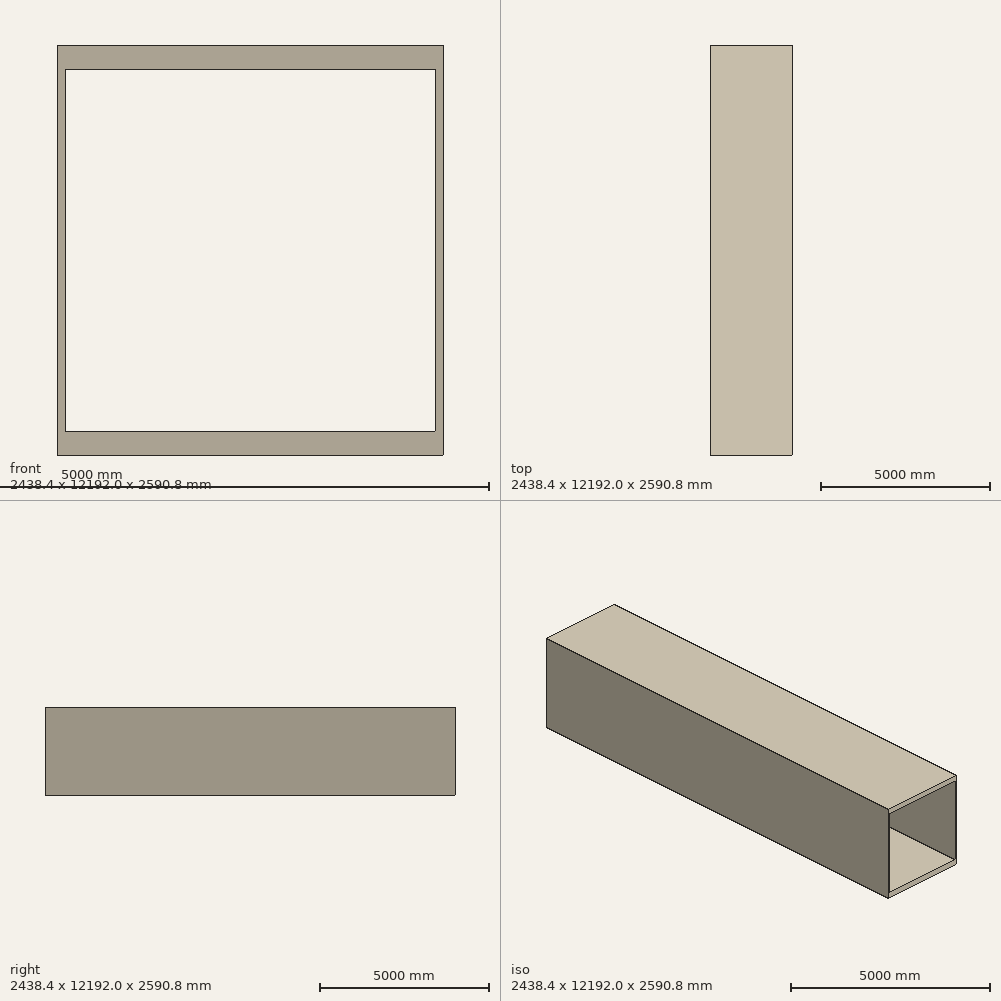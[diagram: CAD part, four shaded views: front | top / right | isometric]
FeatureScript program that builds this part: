
annotation { "Feature Type Name" : "Feature", "Feature Type Description" : "" }
export const myFeature = defineFeature(function(context is Context, id is Id, definition is map)
    precondition{}
    {
        {
            var Q0;
            Q0=qCreatedBy(makeId("Front.planeOp"),FACE);
            var sketch = newSketch(context, id + "F0", { "sketchPlane" : qUnion([Q0])});
            skLineSegment(sketch, "E0.bottom", {"start": v(-1219.2, 0) * mm, "end": v(1219.2, 0) * mm});
            skLineSegment(sketch, "E0.top", {"start": v(-1219.2, 2590.8) * mm, "end": v(1219.2, 2590.8) * mm});
            skLineSegment(sketch, "E0.left", {"start": v(-1219.2, 0) * mm, "end": v(-1219.2, 2590.8) * mm});
            skLineSegment(sketch, "E0.right", {"start": v(1219.2, 0) * mm, "end": v(1219.2, 2590.8) * mm});
            skLineSegment(sketch, "E1.bottom", {"start": v(-1168.4, 2438.4) * mm, "end": v(1168.4, 2438.4) * mm});
            skLineSegment(sketch, "E1.top", {"start": v(-1168.4, 152.4) * mm, "end": v(1168.4, 152.4) * mm});
            skLineSegment(sketch, "E1.left", {"start": v(-1168.4, 2438.4) * mm, "end": v(-1168.4, 152.4) * mm});
            skLineSegment(sketch, "E1.right", {"start": v(1168.4, 2438.4) * mm, "end": v(1168.4, 152.4) * mm});
            skPoint(sketch, "E2.endSnap0", {"position": v(-1168.4, 1295.4) * mm});
            skLineSegment(sketch, "E3", {"start": v(-1168.4, 1295.4) * mm, "end": v(-1219.2, 1295.4) * mm, "construction": true});
            skLineSegment(sketch, "E4", {"start": v(0, 152.4) * mm, "end": v(0, 0) * mm, "construction": true});
            skSolve(sketch);
        }
        {
            var Q0;
            Q0 = qSketchRegion(id + "F0", true);
            extrude(context, id + "F1", {"entities" : qUnion([Q0]), "depth" : 12192 * mm, "offsetDistance" : 25.4 * mm});
        }
    });
